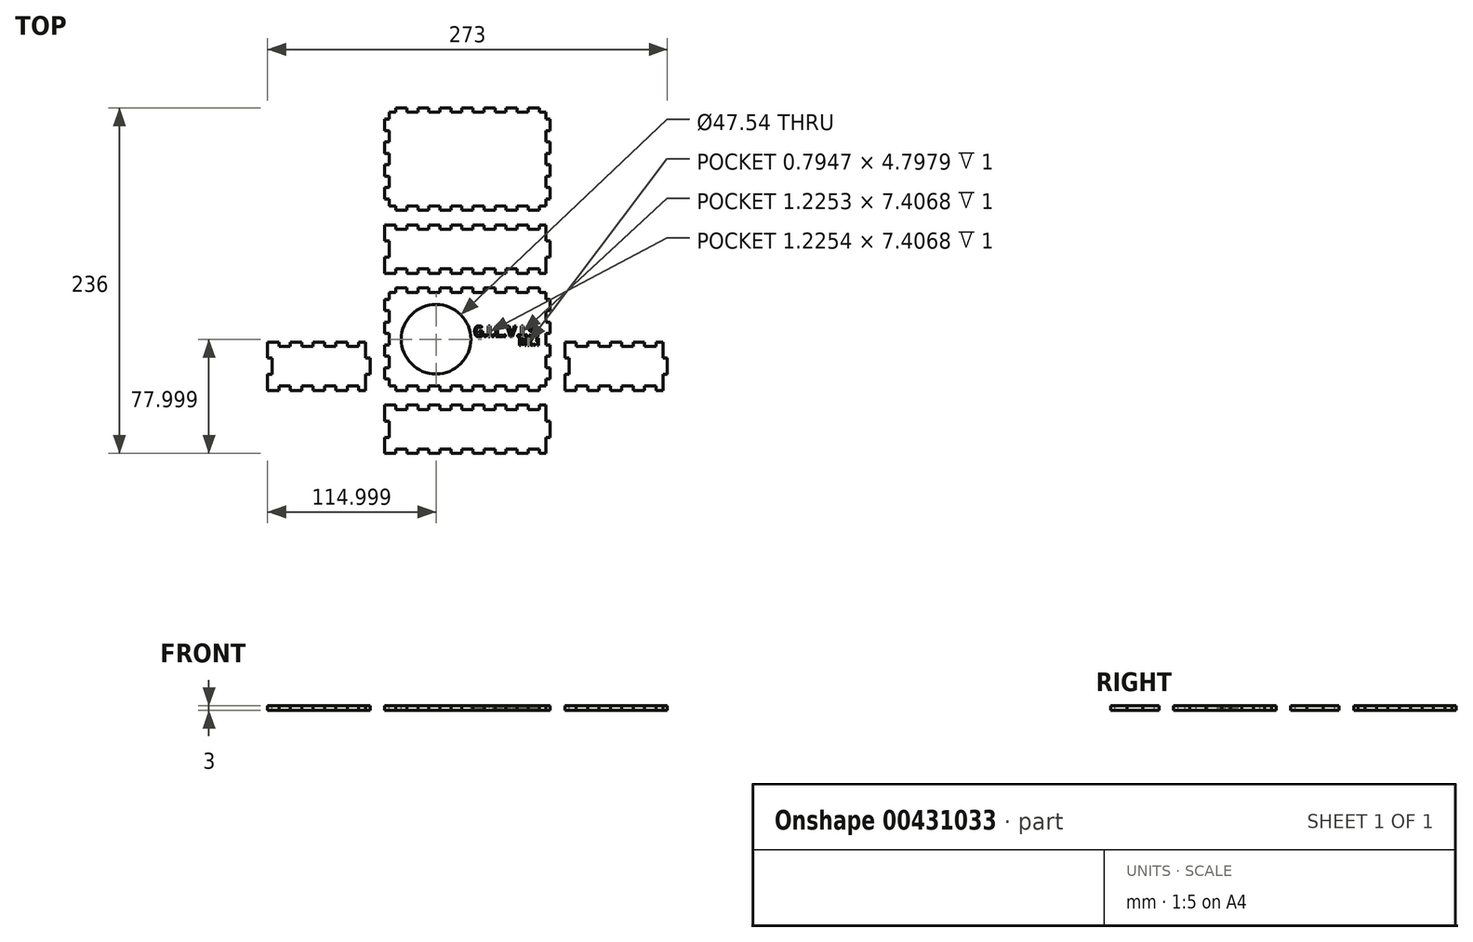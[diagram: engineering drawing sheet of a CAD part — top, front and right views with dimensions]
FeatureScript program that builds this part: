
annotation { "Feature Type Name" : "Feature", "Feature Type Description" : "" }
export const myFeature = defineFeature(function(context is Context, id is Id, definition is map)
    precondition{}
    {
        {
            var Q0;
            Q0=qCreatedBy(makeId("Top.planeOp"),FACE);
            var sketch = newSketch(context, id + "F0", { "sketchPlane" : qUnion([Q0])});
            skLineSegment(sketch, "E0", {"start": v(-136.5, -118) * mm, "end": v(136.5, -118) * mm, "construction": true});
            skLineSegment(sketch, "E1", {"start": v(136.5, -118) * mm, "end": v(136.5, 118) * mm, "construction": true});
            skLineSegment(sketch, "E2", {"start": v(136.5, 118) * mm, "end": v(-136.5, 118) * mm, "construction": true});
            skLineSegment(sketch, "E3", {"start": v(-136.5, 118) * mm, "end": v(-136.5, -118) * mm, "construction": true});
            skLineSegment(sketch, "E4", {"start": v(-56.5, -118) * mm, "end": v(-48.97, -118) * mm});
            skLineSegment(sketch, "E5", {"start": v(-48.97, -115) * mm, "end": v(-48.97, -118) * mm});
            skLineSegment(sketch, "E6", {"start": v(-48.97, -115) * mm, "end": v(-41.43, -115) * mm});
            skLineSegment(sketch, "E7", {"start": v(-41.43, -115) * mm, "end": v(-41.43, -118) * mm});
            skLineSegment(sketch, "E8", {"start": v(-41.43, -118) * mm, "end": v(-33.9, -118) * mm});
            skLineSegment(sketch, "E9", {"start": v(-33.9, -115) * mm, "end": v(-33.9, -118) * mm});
            skLineSegment(sketch, "E10", {"start": v(-33.9, -115) * mm, "end": v(-26.37, -115) * mm});
            skLineSegment(sketch, "E11", {"start": v(-26.37, -115) * mm, "end": v(-26.37, -118) * mm});
            skLineSegment(sketch, "E12", {"start": v(-26.37, -118) * mm, "end": v(-18.83, -118) * mm});
            skLineSegment(sketch, "E13", {"start": v(-18.83, -115) * mm, "end": v(-18.83, -118) * mm});
            skLineSegment(sketch, "E14", {"start": v(-18.83, -115) * mm, "end": v(-11.3, -115) * mm});
            skLineSegment(sketch, "E15", {"start": v(-11.3, -115) * mm, "end": v(-11.3, -118) * mm});
            skLineSegment(sketch, "E16", {"start": v(-11.3, -118) * mm, "end": v(-3.77, -118) * mm});
            skLineSegment(sketch, "E17", {"start": v(-3.77, -115) * mm, "end": v(-3.77, -118) * mm});
            skLineSegment(sketch, "E18", {"start": v(-3.77, -115) * mm, "end": v(3.77, -115) * mm});
            skLineSegment(sketch, "E19", {"start": v(3.77, -115) * mm, "end": v(3.77, -118) * mm});
            skLineSegment(sketch, "E20", {"start": v(3.77, -118) * mm, "end": v(11.3, -118) * mm});
            skLineSegment(sketch, "E21", {"start": v(11.3, -115) * mm, "end": v(11.3, -118) * mm});
            skLineSegment(sketch, "E22", {"start": v(11.3, -115) * mm, "end": v(18.83, -115) * mm});
            skLineSegment(sketch, "E23", {"start": v(18.83, -115) * mm, "end": v(18.83, -118) * mm});
            skLineSegment(sketch, "E24", {"start": v(18.83, -118) * mm, "end": v(26.37, -118) * mm});
            skLineSegment(sketch, "E25", {"start": v(26.37, -115) * mm, "end": v(26.37, -118) * mm});
            skLineSegment(sketch, "E26", {"start": v(26.37, -115) * mm, "end": v(33.9, -115) * mm});
            skLineSegment(sketch, "E27", {"start": v(33.9, -115) * mm, "end": v(33.9, -118) * mm});
            skLineSegment(sketch, "E28", {"start": v(33.9, -118) * mm, "end": v(41.43, -118) * mm});
            skLineSegment(sketch, "E29", {"start": v(41.43, -115) * mm, "end": v(41.43, -118) * mm});
            skLineSegment(sketch, "E30", {"start": v(41.43, -115) * mm, "end": v(48.97, -115) * mm});
            skLineSegment(sketch, "E31", {"start": v(48.97, -115) * mm, "end": v(48.97, -118) * mm});
            skLineSegment(sketch, "E32", {"start": v(48.97, -118) * mm, "end": v(53.5, -118) * mm});
            skLineSegment(sketch, "E33", {"start": v(-56.5, -85) * mm, "end": v(-48.97, -85) * mm});
            skLineSegment(sketch, "E34", {"start": v(-48.97, -85) * mm, "end": v(-48.97, -88) * mm});
            skLineSegment(sketch, "E35", {"start": v(-48.97, -88) * mm, "end": v(-41.43, -88) * mm});
            skLineSegment(sketch, "E36", {"start": v(-41.43, -85) * mm, "end": v(-41.43, -88) * mm});
            skLineSegment(sketch, "E37", {"start": v(-41.43, -85) * mm, "end": v(-33.9, -85) * mm});
            skLineSegment(sketch, "E38", {"start": v(-33.9, -85) * mm, "end": v(-33.9, -88) * mm});
            skLineSegment(sketch, "E39", {"start": v(-33.9, -88) * mm, "end": v(-26.37, -88) * mm});
            skLineSegment(sketch, "E40", {"start": v(-26.37, -85) * mm, "end": v(-26.37, -88) * mm});
            skLineSegment(sketch, "E41", {"start": v(-26.37, -85) * mm, "end": v(-18.83, -85) * mm});
            skLineSegment(sketch, "E42", {"start": v(-18.83, -85) * mm, "end": v(-18.83, -88) * mm});
            skLineSegment(sketch, "E43", {"start": v(-18.83, -88) * mm, "end": v(-11.3, -88) * mm});
            skLineSegment(sketch, "E44", {"start": v(-11.3, -85) * mm, "end": v(-11.3, -88) * mm});
            skLineSegment(sketch, "E45", {"start": v(-11.3, -85) * mm, "end": v(-3.77, -85) * mm});
            skLineSegment(sketch, "E46", {"start": v(-3.77, -85) * mm, "end": v(-3.77, -88) * mm});
            skLineSegment(sketch, "E47", {"start": v(-3.77, -88) * mm, "end": v(3.77, -88) * mm});
            skLineSegment(sketch, "E48", {"start": v(3.77, -85) * mm, "end": v(3.77, -88) * mm});
            skLineSegment(sketch, "E49", {"start": v(3.77, -85) * mm, "end": v(11.3, -85) * mm});
            skLineSegment(sketch, "E50", {"start": v(11.3, -85) * mm, "end": v(11.3, -88) * mm});
            skLineSegment(sketch, "E51", {"start": v(11.3, -88) * mm, "end": v(18.83, -88) * mm});
            skLineSegment(sketch, "E52", {"start": v(18.83, -85) * mm, "end": v(18.83, -88) * mm});
            skLineSegment(sketch, "E53", {"start": v(18.83, -85) * mm, "end": v(26.37, -85) * mm});
            skLineSegment(sketch, "E54", {"start": v(26.37, -85) * mm, "end": v(26.37, -88) * mm});
            skLineSegment(sketch, "E55", {"start": v(26.37, -88) * mm, "end": v(33.9, -88) * mm});
            skLineSegment(sketch, "E56", {"start": v(33.9, -85) * mm, "end": v(33.9, -88) * mm});
            skLineSegment(sketch, "E57", {"start": v(33.9, -85) * mm, "end": v(41.43, -85) * mm});
            skLineSegment(sketch, "E58", {"start": v(41.43, -85) * mm, "end": v(41.43, -88) * mm});
            skLineSegment(sketch, "E59", {"start": v(41.43, -88) * mm, "end": v(48.97, -88) * mm});
            skLineSegment(sketch, "E60", {"start": v(48.97, -85) * mm, "end": v(48.97, -88) * mm});
            skLineSegment(sketch, "E61", {"start": v(48.97, -85) * mm, "end": v(53.5, -85) * mm});
            skLineSegment(sketch, "E62", {"start": v(-56.5, -118) * mm, "end": v(-56.5, -107) * mm});
            skLineSegment(sketch, "E63", {"start": v(-53.5, -107) * mm, "end": v(-56.5, -107) * mm});
            skLineSegment(sketch, "E64", {"start": v(-53.5, -107) * mm, "end": v(-53.5, -96) * mm});
            skLineSegment(sketch, "E65", {"start": v(-53.5, -96) * mm, "end": v(-56.5, -96) * mm});
            skLineSegment(sketch, "E66", {"start": v(-56.5, -96) * mm, "end": v(-56.5, -85) * mm});
            skLineSegment(sketch, "E67", {"start": v(53.5, -118) * mm, "end": v(53.5, -107) * mm});
            skLineSegment(sketch, "E68", {"start": v(56.5, -107) * mm, "end": v(53.5, -107) * mm});
            skLineSegment(sketch, "E69", {"start": v(56.5, -107) * mm, "end": v(56.5, -96) * mm});
            skLineSegment(sketch, "E70", {"start": v(56.5, -96) * mm, "end": v(53.5, -96) * mm});
            skLineSegment(sketch, "E71", {"start": v(53.5, -96) * mm, "end": v(53.5, -85) * mm});
            skLineSegment(sketch, "E72", {"start": v(-136.5, -75) * mm, "end": v(-128.72, -75) * mm});
            skLineSegment(sketch, "E73", {"start": v(-128.72, -72) * mm, "end": v(-128.72, -75) * mm});
            skLineSegment(sketch, "E74", {"start": v(-128.72, -72) * mm, "end": v(-120.94, -72) * mm});
            skLineSegment(sketch, "E75", {"start": v(-120.94, -72) * mm, "end": v(-120.94, -75) * mm});
            skLineSegment(sketch, "E76", {"start": v(-120.94, -75) * mm, "end": v(-113.17, -75) * mm});
            skLineSegment(sketch, "E77", {"start": v(-113.17, -72) * mm, "end": v(-113.17, -75) * mm});
            skLineSegment(sketch, "E78", {"start": v(-113.17, -72) * mm, "end": v(-105.39, -72) * mm});
            skLineSegment(sketch, "E79", {"start": v(-105.39, -72) * mm, "end": v(-105.39, -75) * mm});
            skLineSegment(sketch, "E80", {"start": v(-105.39, -75) * mm, "end": v(-97.61, -75) * mm});
            skLineSegment(sketch, "E81", {"start": v(-97.61, -72) * mm, "end": v(-97.61, -75) * mm});
            skLineSegment(sketch, "E82", {"start": v(-97.61, -72) * mm, "end": v(-89.83, -72) * mm});
            skLineSegment(sketch, "E83", {"start": v(-89.83, -72) * mm, "end": v(-89.83, -75) * mm});
            skLineSegment(sketch, "E84", {"start": v(-89.83, -75) * mm, "end": v(-82.06, -75) * mm});
            skLineSegment(sketch, "E85", {"start": v(-82.06, -72) * mm, "end": v(-82.06, -75) * mm});
            skLineSegment(sketch, "E86", {"start": v(-82.06, -72) * mm, "end": v(-74.28, -72) * mm});
            skLineSegment(sketch, "E87", {"start": v(-74.28, -72) * mm, "end": v(-74.28, -75) * mm});
            skLineSegment(sketch, "E88", {"start": v(-74.28, -75) * mm, "end": v(-69.5, -75) * mm});
            skLineSegment(sketch, "E89", {"start": v(-136.5, -42) * mm, "end": v(-128.72, -42) * mm});
            skLineSegment(sketch, "E90", {"start": v(-128.72, -42) * mm, "end": v(-128.72, -45) * mm});
            skLineSegment(sketch, "E91", {"start": v(-128.72, -45) * mm, "end": v(-120.94, -45) * mm});
            skLineSegment(sketch, "E92", {"start": v(-120.94, -42) * mm, "end": v(-120.94, -45) * mm});
            skLineSegment(sketch, "E93", {"start": v(-120.94, -42) * mm, "end": v(-113.17, -42) * mm});
            skLineSegment(sketch, "E94", {"start": v(-113.17, -42) * mm, "end": v(-113.17, -45) * mm});
            skLineSegment(sketch, "E95", {"start": v(-113.17, -45) * mm, "end": v(-105.39, -45) * mm});
            skLineSegment(sketch, "E96", {"start": v(-105.39, -42) * mm, "end": v(-105.39, -45) * mm});
            skLineSegment(sketch, "E97", {"start": v(-105.39, -42) * mm, "end": v(-97.61, -42) * mm});
            skLineSegment(sketch, "E98", {"start": v(-97.61, -42) * mm, "end": v(-97.61, -45) * mm});
            skLineSegment(sketch, "E99", {"start": v(-97.61, -45) * mm, "end": v(-89.83, -45) * mm});
            skLineSegment(sketch, "E100", {"start": v(-89.83, -42) * mm, "end": v(-89.83, -45) * mm});
            skLineSegment(sketch, "E101", {"start": v(-89.83, -42) * mm, "end": v(-82.06, -42) * mm});
            skLineSegment(sketch, "E102", {"start": v(-82.06, -42) * mm, "end": v(-82.06, -45) * mm});
            skLineSegment(sketch, "E103", {"start": v(-82.06, -45) * mm, "end": v(-74.28, -45) * mm});
            skLineSegment(sketch, "E104", {"start": v(-74.28, -42) * mm, "end": v(-74.28, -45) * mm});
            skLineSegment(sketch, "E105", {"start": v(-74.28, -42) * mm, "end": v(-69.5, -42) * mm});
            skLineSegment(sketch, "E106", {"start": v(-136.5, -75) * mm, "end": v(-136.5, -64) * mm});
            skLineSegment(sketch, "E107", {"start": v(-133.5, -64) * mm, "end": v(-136.5, -64) * mm});
            skLineSegment(sketch, "E108", {"start": v(-133.5, -64) * mm, "end": v(-133.5, -53) * mm});
            skLineSegment(sketch, "E109", {"start": v(-133.5, -53) * mm, "end": v(-136.5, -53) * mm});
            skLineSegment(sketch, "E110", {"start": v(-136.5, -53) * mm, "end": v(-136.5, -42) * mm});
            skLineSegment(sketch, "E111", {"start": v(-69.5, -75) * mm, "end": v(-69.5, -64) * mm});
            skLineSegment(sketch, "E112", {"start": v(-66.5, -64) * mm, "end": v(-69.5, -64) * mm});
            skLineSegment(sketch, "E113", {"start": v(-66.5, -64) * mm, "end": v(-66.5, -53) * mm});
            skLineSegment(sketch, "E114", {"start": v(-66.5, -53) * mm, "end": v(-69.5, -53) * mm});
            skLineSegment(sketch, "E115", {"start": v(-69.5, -53) * mm, "end": v(-69.5, -42) * mm});
            skLineSegment(sketch, "E116", {"start": v(-53.5, -72) * mm, "end": v(-48.97, -72) * mm});
            skLineSegment(sketch, "E117", {"start": v(-48.97, -72) * mm, "end": v(-48.97, -75) * mm});
            skLineSegment(sketch, "E118", {"start": v(-48.97, -75) * mm, "end": v(-41.43, -75) * mm});
            skLineSegment(sketch, "E119", {"start": v(-41.43, -72) * mm, "end": v(-41.43, -75) * mm});
            skLineSegment(sketch, "E120", {"start": v(-41.43, -72) * mm, "end": v(-33.9, -72) * mm});
            skLineSegment(sketch, "E121", {"start": v(-33.9, -72) * mm, "end": v(-33.9, -75) * mm});
            skLineSegment(sketch, "E122", {"start": v(-33.9, -75) * mm, "end": v(-26.37, -75) * mm});
            skLineSegment(sketch, "E123", {"start": v(-26.37, -72) * mm, "end": v(-26.37, -75) * mm});
            skLineSegment(sketch, "E124", {"start": v(-26.37, -72) * mm, "end": v(-18.83, -72) * mm});
            skLineSegment(sketch, "E125", {"start": v(-18.83, -72) * mm, "end": v(-18.83, -75) * mm});
            skLineSegment(sketch, "E126", {"start": v(-18.83, -75) * mm, "end": v(-11.3, -75) * mm});
            skLineSegment(sketch, "E127", {"start": v(-11.3, -72) * mm, "end": v(-11.3, -75) * mm});
            skLineSegment(sketch, "E128", {"start": v(-11.3, -72) * mm, "end": v(-3.77, -72) * mm});
            skLineSegment(sketch, "E129", {"start": v(-3.77, -72) * mm, "end": v(-3.77, -75) * mm});
            skLineSegment(sketch, "E130", {"start": v(-3.77, -75) * mm, "end": v(3.77, -75) * mm});
            skLineSegment(sketch, "E131", {"start": v(3.77, -72) * mm, "end": v(3.77, -75) * mm});
            skLineSegment(sketch, "E132", {"start": v(3.77, -72) * mm, "end": v(11.3, -72) * mm});
            skLineSegment(sketch, "E133", {"start": v(11.3, -72) * mm, "end": v(11.3, -75) * mm});
            skLineSegment(sketch, "E134", {"start": v(11.3, -75) * mm, "end": v(18.83, -75) * mm});
            skLineSegment(sketch, "E135", {"start": v(18.83, -72) * mm, "end": v(18.83, -75) * mm});
            skLineSegment(sketch, "E136", {"start": v(18.83, -72) * mm, "end": v(26.37, -72) * mm});
            skLineSegment(sketch, "E137", {"start": v(26.37, -72) * mm, "end": v(26.37, -75) * mm});
            skLineSegment(sketch, "E138", {"start": v(26.37, -75) * mm, "end": v(33.9, -75) * mm});
            skLineSegment(sketch, "E139", {"start": v(33.9, -72) * mm, "end": v(33.9, -75) * mm});
            skLineSegment(sketch, "E140", {"start": v(33.9, -72) * mm, "end": v(41.43, -72) * mm});
            skLineSegment(sketch, "E141", {"start": v(41.43, -72) * mm, "end": v(41.43, -75) * mm});
            skLineSegment(sketch, "E142", {"start": v(41.43, -75) * mm, "end": v(48.97, -75) * mm});
            skLineSegment(sketch, "E143", {"start": v(48.97, -72) * mm, "end": v(48.97, -75) * mm});
            skLineSegment(sketch, "E144", {"start": v(48.97, -72) * mm, "end": v(53.5, -72) * mm});
            skLineSegment(sketch, "E145", {"start": v(-53.5, -8) * mm, "end": v(-48.97, -8) * mm});
            skLineSegment(sketch, "E146", {"start": v(-48.97, -5) * mm, "end": v(-48.97, -8) * mm});
            skLineSegment(sketch, "E147", {"start": v(-48.97, -5) * mm, "end": v(-41.43, -5) * mm});
            skLineSegment(sketch, "E148", {"start": v(-41.43, -5) * mm, "end": v(-41.43, -8) * mm});
            skLineSegment(sketch, "E149", {"start": v(-41.43, -8) * mm, "end": v(-33.9, -8) * mm});
            skLineSegment(sketch, "E150", {"start": v(-33.9, -5) * mm, "end": v(-33.9, -8) * mm});
            skLineSegment(sketch, "E151", {"start": v(-33.9, -5) * mm, "end": v(-26.37, -5) * mm});
            skLineSegment(sketch, "E152", {"start": v(-26.37, -5) * mm, "end": v(-26.37, -8) * mm});
            skLineSegment(sketch, "E153", {"start": v(-26.37, -8) * mm, "end": v(-18.83, -8) * mm});
            skLineSegment(sketch, "E154", {"start": v(-18.83, -5) * mm, "end": v(-18.83, -8) * mm});
            skLineSegment(sketch, "E155", {"start": v(-18.83, -5) * mm, "end": v(-11.3, -5) * mm});
            skLineSegment(sketch, "E156", {"start": v(-11.3, -5) * mm, "end": v(-11.3, -8) * mm});
            skLineSegment(sketch, "E157", {"start": v(-11.3, -8) * mm, "end": v(-3.77, -8) * mm});
            skLineSegment(sketch, "E158", {"start": v(-3.77, -5) * mm, "end": v(-3.77, -8) * mm});
            skLineSegment(sketch, "E159", {"start": v(-3.77, -5) * mm, "end": v(3.77, -5) * mm});
            skLineSegment(sketch, "E160", {"start": v(3.77, -5) * mm, "end": v(3.77, -8) * mm});
            skLineSegment(sketch, "E161", {"start": v(3.77, -8) * mm, "end": v(11.3, -8) * mm});
            skLineSegment(sketch, "E162", {"start": v(11.3, -5) * mm, "end": v(11.3, -8) * mm});
            skLineSegment(sketch, "E163", {"start": v(11.3, -5) * mm, "end": v(18.83, -5) * mm});
            skLineSegment(sketch, "E164", {"start": v(18.83, -5) * mm, "end": v(18.83, -8) * mm});
            skLineSegment(sketch, "E165", {"start": v(18.83, -8) * mm, "end": v(26.37, -8) * mm});
            skLineSegment(sketch, "E166", {"start": v(26.37, -5) * mm, "end": v(26.37, -8) * mm});
            skLineSegment(sketch, "E167", {"start": v(26.37, -5) * mm, "end": v(33.9, -5) * mm});
            skLineSegment(sketch, "E168", {"start": v(33.9, -5) * mm, "end": v(33.9, -8) * mm});
            skLineSegment(sketch, "E169", {"start": v(33.9, -8) * mm, "end": v(41.43, -8) * mm});
            skLineSegment(sketch, "E170", {"start": v(41.43, -5) * mm, "end": v(41.43, -8) * mm});
            skLineSegment(sketch, "E171", {"start": v(41.43, -5) * mm, "end": v(48.97, -5) * mm});
            skLineSegment(sketch, "E172", {"start": v(48.97, -5) * mm, "end": v(48.97, -8) * mm});
            skLineSegment(sketch, "E173", {"start": v(48.97, -8) * mm, "end": v(53.5, -8) * mm});
            skLineSegment(sketch, "E174", {"start": v(-53.5, -72) * mm, "end": v(-53.5, -67.22) * mm});
            skLineSegment(sketch, "E175", {"start": v(-53.5, -67.22) * mm, "end": v(-56.5, -67.22) * mm});
            skLineSegment(sketch, "E176", {"start": v(-56.5, -67.22) * mm, "end": v(-56.5, -59.44) * mm});
            skLineSegment(sketch, "E177", {"start": v(-53.5, -59.44) * mm, "end": v(-56.5, -59.44) * mm});
            skLineSegment(sketch, "E178", {"start": v(-53.5, -59.44) * mm, "end": v(-53.5, -51.67) * mm});
            skLineSegment(sketch, "E179", {"start": v(-53.5, -51.67) * mm, "end": v(-56.5, -51.67) * mm});
            skLineSegment(sketch, "E180", {"start": v(-56.5, -51.67) * mm, "end": v(-56.5, -43.89) * mm});
            skLineSegment(sketch, "E181", {"start": v(-53.5, -43.89) * mm, "end": v(-56.5, -43.89) * mm});
            skLineSegment(sketch, "E182", {"start": v(-53.5, -43.89) * mm, "end": v(-53.5, -36.11) * mm});
            skLineSegment(sketch, "E183", {"start": v(-53.5, -36.11) * mm, "end": v(-56.5, -36.11) * mm});
            skLineSegment(sketch, "E184", {"start": v(-56.5, -36.11) * mm, "end": v(-56.5, -28.33) * mm});
            skLineSegment(sketch, "E185", {"start": v(-53.5, -28.33) * mm, "end": v(-56.5, -28.33) * mm});
            skLineSegment(sketch, "E186", {"start": v(-53.5, -28.33) * mm, "end": v(-53.5, -20.56) * mm});
            skLineSegment(sketch, "E187", {"start": v(-53.5, -20.56) * mm, "end": v(-56.5, -20.56) * mm});
            skLineSegment(sketch, "E188", {"start": v(-56.5, -20.56) * mm, "end": v(-56.5, -12.78) * mm});
            skLineSegment(sketch, "E189", {"start": v(-53.5, -12.78) * mm, "end": v(-56.5, -12.78) * mm});
            skLineSegment(sketch, "E190", {"start": v(-53.5, -12.78) * mm, "end": v(-53.5, -8) * mm});
            skLineSegment(sketch, "E191", {"start": v(53.5, -72) * mm, "end": v(53.5, -67.22) * mm});
            skLineSegment(sketch, "E192", {"start": v(56.5, -67.22) * mm, "end": v(53.5, -67.22) * mm});
            skLineSegment(sketch, "E193", {"start": v(56.5, -67.22) * mm, "end": v(56.5, -59.44) * mm});
            skLineSegment(sketch, "E194", {"start": v(56.5, -59.44) * mm, "end": v(53.5, -59.44) * mm});
            skLineSegment(sketch, "E195", {"start": v(53.5, -59.44) * mm, "end": v(53.5, -51.67) * mm});
            skLineSegment(sketch, "E196", {"start": v(56.5, -51.67) * mm, "end": v(53.5, -51.67) * mm});
            skLineSegment(sketch, "E197", {"start": v(56.5, -51.67) * mm, "end": v(56.5, -43.89) * mm});
            skLineSegment(sketch, "E198", {"start": v(56.5, -43.89) * mm, "end": v(53.5, -43.89) * mm});
            skLineSegment(sketch, "E199", {"start": v(53.5, -43.89) * mm, "end": v(53.5, -36.11) * mm});
            skLineSegment(sketch, "E200", {"start": v(56.5, -36.11) * mm, "end": v(53.5, -36.11) * mm});
            skLineSegment(sketch, "E201", {"start": v(56.5, -36.11) * mm, "end": v(56.5, -28.33) * mm});
            skLineSegment(sketch, "E202", {"start": v(56.5, -28.33) * mm, "end": v(53.5, -28.33) * mm});
            skLineSegment(sketch, "E203", {"start": v(53.5, -28.33) * mm, "end": v(53.5, -20.56) * mm});
            skLineSegment(sketch, "E204", {"start": v(56.5, -20.56) * mm, "end": v(53.5, -20.56) * mm});
            skLineSegment(sketch, "E205", {"start": v(56.5, -20.56) * mm, "end": v(56.5, -12.78) * mm});
            skLineSegment(sketch, "E206", {"start": v(56.5, -12.78) * mm, "end": v(53.5, -12.78) * mm});
            skLineSegment(sketch, "E207", {"start": v(53.5, -12.78) * mm, "end": v(53.5, -8) * mm});
            skLineSegment(sketch, "E208", {"start": v(66.5, -75) * mm, "end": v(74.28, -75) * mm});
            skLineSegment(sketch, "E209", {"start": v(74.28, -72) * mm, "end": v(74.28, -75) * mm});
            skLineSegment(sketch, "E210", {"start": v(74.28, -72) * mm, "end": v(82.06, -72) * mm});
            skLineSegment(sketch, "E211", {"start": v(82.06, -72) * mm, "end": v(82.06, -75) * mm});
            skLineSegment(sketch, "E212", {"start": v(82.06, -75) * mm, "end": v(89.83, -75) * mm});
            skLineSegment(sketch, "E213", {"start": v(89.83, -72) * mm, "end": v(89.83, -75) * mm});
            skLineSegment(sketch, "E214", {"start": v(89.83, -72) * mm, "end": v(97.61, -72) * mm});
            skLineSegment(sketch, "E215", {"start": v(97.61, -72) * mm, "end": v(97.61, -75) * mm});
            skLineSegment(sketch, "E216", {"start": v(97.61, -75) * mm, "end": v(105.39, -75) * mm});
            skLineSegment(sketch, "E217", {"start": v(105.39, -72) * mm, "end": v(105.39, -75) * mm});
            skLineSegment(sketch, "E218", {"start": v(105.39, -72) * mm, "end": v(113.17, -72) * mm});
            skLineSegment(sketch, "E219", {"start": v(113.17, -72) * mm, "end": v(113.17, -75) * mm});
            skLineSegment(sketch, "E220", {"start": v(113.17, -75) * mm, "end": v(120.94, -75) * mm});
            skLineSegment(sketch, "E221", {"start": v(120.94, -72) * mm, "end": v(120.94, -75) * mm});
            skLineSegment(sketch, "E222", {"start": v(120.94, -72) * mm, "end": v(128.72, -72) * mm});
            skLineSegment(sketch, "E223", {"start": v(128.72, -72) * mm, "end": v(128.72, -75) * mm});
            skLineSegment(sketch, "E224", {"start": v(128.72, -75) * mm, "end": v(133.5, -75) * mm});
            skLineSegment(sketch, "E225", {"start": v(66.5, -42) * mm, "end": v(74.28, -42) * mm});
            skLineSegment(sketch, "E226", {"start": v(74.28, -42) * mm, "end": v(74.28, -45) * mm});
            skLineSegment(sketch, "E227", {"start": v(74.28, -45) * mm, "end": v(82.06, -45) * mm});
            skLineSegment(sketch, "E228", {"start": v(82.06, -42) * mm, "end": v(82.06, -45) * mm});
            skLineSegment(sketch, "E229", {"start": v(82.06, -42) * mm, "end": v(89.83, -42) * mm});
            skLineSegment(sketch, "E230", {"start": v(89.83, -42) * mm, "end": v(89.83, -45) * mm});
            skLineSegment(sketch, "E231", {"start": v(89.83, -45) * mm, "end": v(97.61, -45) * mm});
            skLineSegment(sketch, "E232", {"start": v(97.61, -42) * mm, "end": v(97.61, -45) * mm});
            skLineSegment(sketch, "E233", {"start": v(97.61, -42) * mm, "end": v(105.39, -42) * mm});
            skLineSegment(sketch, "E234", {"start": v(105.39, -42) * mm, "end": v(105.39, -45) * mm});
            skLineSegment(sketch, "E235", {"start": v(105.39, -45) * mm, "end": v(113.17, -45) * mm});
            skLineSegment(sketch, "E236", {"start": v(113.17, -42) * mm, "end": v(113.17, -45) * mm});
            skLineSegment(sketch, "E237", {"start": v(113.17, -42) * mm, "end": v(120.94, -42) * mm});
            skLineSegment(sketch, "E238", {"start": v(120.94, -42) * mm, "end": v(120.94, -45) * mm});
            skLineSegment(sketch, "E239", {"start": v(120.94, -45) * mm, "end": v(128.72, -45) * mm});
            skLineSegment(sketch, "E240", {"start": v(128.72, -42) * mm, "end": v(128.72, -45) * mm});
            skLineSegment(sketch, "E241", {"start": v(128.72, -42) * mm, "end": v(133.5, -42) * mm});
            skLineSegment(sketch, "E242", {"start": v(66.5, -75) * mm, "end": v(66.5, -64) * mm});
            skLineSegment(sketch, "E243", {"start": v(69.5, -64) * mm, "end": v(66.5, -64) * mm});
            skLineSegment(sketch, "E244", {"start": v(69.5, -64) * mm, "end": v(69.5, -53) * mm});
            skLineSegment(sketch, "E245", {"start": v(69.5, -53) * mm, "end": v(66.5, -53) * mm});
            skLineSegment(sketch, "E246", {"start": v(66.5, -53) * mm, "end": v(66.5, -42) * mm});
            skLineSegment(sketch, "E247", {"start": v(133.5, -75) * mm, "end": v(133.5, -64) * mm});
            skLineSegment(sketch, "E248", {"start": v(136.5, -64) * mm, "end": v(133.5, -64) * mm});
            skLineSegment(sketch, "E249", {"start": v(136.5, -64) * mm, "end": v(136.5, -53) * mm});
            skLineSegment(sketch, "E250", {"start": v(136.5, -53) * mm, "end": v(133.5, -53) * mm});
            skLineSegment(sketch, "E251", {"start": v(133.5, -53) * mm, "end": v(133.5, -42) * mm});
            skLineSegment(sketch, "E252", {"start": v(-56.5, 5) * mm, "end": v(-48.97, 5) * mm});
            skLineSegment(sketch, "E253", {"start": v(-48.97, 8) * mm, "end": v(-48.97, 5) * mm});
            skLineSegment(sketch, "E254", {"start": v(-48.97, 8) * mm, "end": v(-41.43, 8) * mm});
            skLineSegment(sketch, "E255", {"start": v(-41.43, 8) * mm, "end": v(-41.43, 5) * mm});
            skLineSegment(sketch, "E256", {"start": v(-41.43, 5) * mm, "end": v(-33.9, 5) * mm});
            skLineSegment(sketch, "E257", {"start": v(-33.9, 8) * mm, "end": v(-33.9, 5) * mm});
            skLineSegment(sketch, "E258", {"start": v(-33.9, 8) * mm, "end": v(-26.37, 8) * mm});
            skLineSegment(sketch, "E259", {"start": v(-26.37, 8) * mm, "end": v(-26.37, 5) * mm});
            skLineSegment(sketch, "E260", {"start": v(-26.37, 5) * mm, "end": v(-18.83, 5) * mm});
            skLineSegment(sketch, "E261", {"start": v(-18.83, 8) * mm, "end": v(-18.83, 5) * mm});
            skLineSegment(sketch, "E262", {"start": v(-18.83, 8) * mm, "end": v(-11.3, 8) * mm});
            skLineSegment(sketch, "E263", {"start": v(-11.3, 8) * mm, "end": v(-11.3, 5) * mm});
            skLineSegment(sketch, "E264", {"start": v(-11.3, 5) * mm, "end": v(-3.77, 5) * mm});
            skLineSegment(sketch, "E265", {"start": v(-3.77, 8) * mm, "end": v(-3.77, 5) * mm});
            skLineSegment(sketch, "E266", {"start": v(-3.77, 8) * mm, "end": v(3.77, 8) * mm});
            skLineSegment(sketch, "E267", {"start": v(3.77, 8) * mm, "end": v(3.77, 5) * mm});
            skLineSegment(sketch, "E268", {"start": v(3.77, 5) * mm, "end": v(11.3, 5) * mm});
            skLineSegment(sketch, "E269", {"start": v(11.3, 8) * mm, "end": v(11.3, 5) * mm});
            skLineSegment(sketch, "E270", {"start": v(11.3, 8) * mm, "end": v(18.83, 8) * mm});
            skLineSegment(sketch, "E271", {"start": v(18.83, 8) * mm, "end": v(18.83, 5) * mm});
            skLineSegment(sketch, "E272", {"start": v(18.83, 5) * mm, "end": v(26.37, 5) * mm});
            skLineSegment(sketch, "E273", {"start": v(26.37, 8) * mm, "end": v(26.37, 5) * mm});
            skLineSegment(sketch, "E274", {"start": v(26.37, 8) * mm, "end": v(33.9, 8) * mm});
            skLineSegment(sketch, "E275", {"start": v(33.9, 8) * mm, "end": v(33.9, 5) * mm});
            skLineSegment(sketch, "E276", {"start": v(33.9, 5) * mm, "end": v(41.43, 5) * mm});
            skLineSegment(sketch, "E277", {"start": v(41.43, 8) * mm, "end": v(41.43, 5) * mm});
            skLineSegment(sketch, "E278", {"start": v(41.43, 8) * mm, "end": v(48.97, 8) * mm});
            skLineSegment(sketch, "E279", {"start": v(48.97, 8) * mm, "end": v(48.97, 5) * mm});
            skLineSegment(sketch, "E280", {"start": v(48.97, 5) * mm, "end": v(53.5, 5) * mm});
            skLineSegment(sketch, "E281", {"start": v(-56.5, 38) * mm, "end": v(-48.97, 38) * mm});
            skLineSegment(sketch, "E282", {"start": v(-48.97, 38) * mm, "end": v(-48.97, 35) * mm});
            skLineSegment(sketch, "E283", {"start": v(-48.97, 35) * mm, "end": v(-41.43, 35) * mm});
            skLineSegment(sketch, "E284", {"start": v(-41.43, 38) * mm, "end": v(-41.43, 35) * mm});
            skLineSegment(sketch, "E285", {"start": v(-41.43, 38) * mm, "end": v(-33.9, 38) * mm});
            skLineSegment(sketch, "E286", {"start": v(-33.9, 38) * mm, "end": v(-33.9, 35) * mm});
            skLineSegment(sketch, "E287", {"start": v(-33.9, 35) * mm, "end": v(-26.37, 35) * mm});
            skLineSegment(sketch, "E288", {"start": v(-26.37, 38) * mm, "end": v(-26.37, 35) * mm});
            skLineSegment(sketch, "E289", {"start": v(-26.37, 38) * mm, "end": v(-18.83, 38) * mm});
            skLineSegment(sketch, "E290", {"start": v(-18.83, 38) * mm, "end": v(-18.83, 35) * mm});
            skLineSegment(sketch, "E291", {"start": v(-18.83, 35) * mm, "end": v(-11.3, 35) * mm});
            skLineSegment(sketch, "E292", {"start": v(-11.3, 38) * mm, "end": v(-11.3, 35) * mm});
            skLineSegment(sketch, "E293", {"start": v(-11.3, 38) * mm, "end": v(-3.77, 38) * mm});
            skLineSegment(sketch, "E294", {"start": v(-3.77, 38) * mm, "end": v(-3.77, 35) * mm});
            skLineSegment(sketch, "E295", {"start": v(-3.77, 35) * mm, "end": v(3.77, 35) * mm});
            skLineSegment(sketch, "E296", {"start": v(3.77, 38) * mm, "end": v(3.77, 35) * mm});
            skLineSegment(sketch, "E297", {"start": v(3.77, 38) * mm, "end": v(11.3, 38) * mm});
            skLineSegment(sketch, "E298", {"start": v(11.3, 38) * mm, "end": v(11.3, 35) * mm});
            skLineSegment(sketch, "E299", {"start": v(11.3, 35) * mm, "end": v(18.83, 35) * mm});
            skLineSegment(sketch, "E300", {"start": v(18.83, 38) * mm, "end": v(18.83, 35) * mm});
            skLineSegment(sketch, "E301", {"start": v(18.83, 38) * mm, "end": v(26.37, 38) * mm});
            skLineSegment(sketch, "E302", {"start": v(26.37, 38) * mm, "end": v(26.37, 35) * mm});
            skLineSegment(sketch, "E303", {"start": v(26.37, 35) * mm, "end": v(33.9, 35) * mm});
            skLineSegment(sketch, "E304", {"start": v(33.9, 38) * mm, "end": v(33.9, 35) * mm});
            skLineSegment(sketch, "E305", {"start": v(33.9, 38) * mm, "end": v(41.43, 38) * mm});
            skLineSegment(sketch, "E306", {"start": v(41.43, 38) * mm, "end": v(41.43, 35) * mm});
            skLineSegment(sketch, "E307", {"start": v(41.43, 35) * mm, "end": v(48.97, 35) * mm});
            skLineSegment(sketch, "E308", {"start": v(48.97, 38) * mm, "end": v(48.97, 35) * mm});
            skLineSegment(sketch, "E309", {"start": v(48.97, 38) * mm, "end": v(53.5, 38) * mm});
            skLineSegment(sketch, "E310", {"start": v(-56.5, 5) * mm, "end": v(-56.5, 16) * mm});
            skLineSegment(sketch, "E311", {"start": v(-53.5, 16) * mm, "end": v(-56.5, 16) * mm});
            skLineSegment(sketch, "E312", {"start": v(-53.5, 16) * mm, "end": v(-53.5, 27) * mm});
            skLineSegment(sketch, "E313", {"start": v(-53.5, 27) * mm, "end": v(-56.5, 27) * mm});
            skLineSegment(sketch, "E314", {"start": v(-56.5, 27) * mm, "end": v(-56.5, 38) * mm});
            skLineSegment(sketch, "E315", {"start": v(53.5, 5) * mm, "end": v(53.5, 16) * mm});
            skLineSegment(sketch, "E316", {"start": v(56.5, 16) * mm, "end": v(53.5, 16) * mm});
            skLineSegment(sketch, "E317", {"start": v(56.5, 16) * mm, "end": v(56.5, 27) * mm});
            skLineSegment(sketch, "E318", {"start": v(56.5, 27) * mm, "end": v(53.5, 27) * mm});
            skLineSegment(sketch, "E319", {"start": v(53.5, 27) * mm, "end": v(53.5, 38) * mm});
            skLineSegment(sketch, "E320", {"start": v(-53.5, 51) * mm, "end": v(-48.97, 51) * mm});
            skLineSegment(sketch, "E321", {"start": v(-48.97, 51) * mm, "end": v(-48.97, 48) * mm});
            skLineSegment(sketch, "E322", {"start": v(-48.97, 48) * mm, "end": v(-41.43, 48) * mm});
            skLineSegment(sketch, "E323", {"start": v(-41.43, 51) * mm, "end": v(-41.43, 48) * mm});
            skLineSegment(sketch, "E324", {"start": v(-41.43, 51) * mm, "end": v(-33.9, 51) * mm});
            skLineSegment(sketch, "E325", {"start": v(-33.9, 51) * mm, "end": v(-33.9, 48) * mm});
            skLineSegment(sketch, "E326", {"start": v(-33.9, 48) * mm, "end": v(-26.37, 48) * mm});
            skLineSegment(sketch, "E327", {"start": v(-26.37, 51) * mm, "end": v(-26.37, 48) * mm});
            skLineSegment(sketch, "E328", {"start": v(-26.37, 51) * mm, "end": v(-18.83, 51) * mm});
            skLineSegment(sketch, "E329", {"start": v(-18.83, 51) * mm, "end": v(-18.83, 48) * mm});
            skLineSegment(sketch, "E330", {"start": v(-18.83, 48) * mm, "end": v(-11.3, 48) * mm});
            skLineSegment(sketch, "E331", {"start": v(-11.3, 51) * mm, "end": v(-11.3, 48) * mm});
            skLineSegment(sketch, "E332", {"start": v(-11.3, 51) * mm, "end": v(-3.77, 51) * mm});
            skLineSegment(sketch, "E333", {"start": v(-3.77, 51) * mm, "end": v(-3.77, 48) * mm});
            skLineSegment(sketch, "E334", {"start": v(-3.77, 48) * mm, "end": v(3.77, 48) * mm});
            skLineSegment(sketch, "E335", {"start": v(3.77, 51) * mm, "end": v(3.77, 48) * mm});
            skLineSegment(sketch, "E336", {"start": v(3.77, 51) * mm, "end": v(11.3, 51) * mm});
            skLineSegment(sketch, "E337", {"start": v(11.3, 51) * mm, "end": v(11.3, 48) * mm});
            skLineSegment(sketch, "E338", {"start": v(11.3, 48) * mm, "end": v(18.83, 48) * mm});
            skLineSegment(sketch, "E339", {"start": v(18.83, 51) * mm, "end": v(18.83, 48) * mm});
            skLineSegment(sketch, "E340", {"start": v(18.83, 51) * mm, "end": v(26.37, 51) * mm});
            skLineSegment(sketch, "E341", {"start": v(26.37, 51) * mm, "end": v(26.37, 48) * mm});
            skLineSegment(sketch, "E342", {"start": v(26.37, 48) * mm, "end": v(33.9, 48) * mm});
            skLineSegment(sketch, "E343", {"start": v(33.9, 51) * mm, "end": v(33.9, 48) * mm});
            skLineSegment(sketch, "E344", {"start": v(33.9, 51) * mm, "end": v(41.43, 51) * mm});
            skLineSegment(sketch, "E345", {"start": v(41.43, 51) * mm, "end": v(41.43, 48) * mm});
            skLineSegment(sketch, "E346", {"start": v(41.43, 48) * mm, "end": v(48.97, 48) * mm});
            skLineSegment(sketch, "E347", {"start": v(48.97, 51) * mm, "end": v(48.97, 48) * mm});
            skLineSegment(sketch, "E348", {"start": v(48.97, 51) * mm, "end": v(53.5, 51) * mm});
            skLineSegment(sketch, "E349", {"start": v(-53.5, 115) * mm, "end": v(-48.97, 115) * mm});
            skLineSegment(sketch, "E350", {"start": v(-48.97, 118) * mm, "end": v(-48.97, 115) * mm});
            skLineSegment(sketch, "E351", {"start": v(-48.97, 118) * mm, "end": v(-41.43, 118) * mm});
            skLineSegment(sketch, "E352", {"start": v(-41.43, 118) * mm, "end": v(-41.43, 115) * mm});
            skLineSegment(sketch, "E353", {"start": v(-41.43, 115) * mm, "end": v(-33.9, 115) * mm});
            skLineSegment(sketch, "E354", {"start": v(-33.9, 118) * mm, "end": v(-33.9, 115) * mm});
            skLineSegment(sketch, "E355", {"start": v(-33.9, 118) * mm, "end": v(-26.37, 118) * mm});
            skLineSegment(sketch, "E356", {"start": v(-26.37, 118) * mm, "end": v(-26.37, 115) * mm});
            skLineSegment(sketch, "E357", {"start": v(-26.37, 115) * mm, "end": v(-18.83, 115) * mm});
            skLineSegment(sketch, "E358", {"start": v(-18.83, 118) * mm, "end": v(-18.83, 115) * mm});
            skLineSegment(sketch, "E359", {"start": v(-18.83, 118) * mm, "end": v(-11.3, 118) * mm});
            skLineSegment(sketch, "E360", {"start": v(-11.3, 118) * mm, "end": v(-11.3, 115) * mm});
            skLineSegment(sketch, "E361", {"start": v(-11.3, 115) * mm, "end": v(-3.77, 115) * mm});
            skLineSegment(sketch, "E362", {"start": v(-3.77, 118) * mm, "end": v(-3.77, 115) * mm});
            skLineSegment(sketch, "E363", {"start": v(-3.77, 118) * mm, "end": v(3.77, 118) * mm});
            skLineSegment(sketch, "E364", {"start": v(3.77, 118) * mm, "end": v(3.77, 115) * mm});
            skLineSegment(sketch, "E365", {"start": v(3.77, 115) * mm, "end": v(11.3, 115) * mm});
            skLineSegment(sketch, "E366", {"start": v(11.3, 118) * mm, "end": v(11.3, 115) * mm});
            skLineSegment(sketch, "E367", {"start": v(11.3, 118) * mm, "end": v(18.83, 118) * mm});
            skLineSegment(sketch, "E368", {"start": v(18.83, 118) * mm, "end": v(18.83, 115) * mm});
            skLineSegment(sketch, "E369", {"start": v(18.83, 115) * mm, "end": v(26.37, 115) * mm});
            skLineSegment(sketch, "E370", {"start": v(26.37, 118) * mm, "end": v(26.37, 115) * mm});
            skLineSegment(sketch, "E371", {"start": v(26.37, 118) * mm, "end": v(33.9, 118) * mm});
            skLineSegment(sketch, "E372", {"start": v(33.9, 118) * mm, "end": v(33.9, 115) * mm});
            skLineSegment(sketch, "E373", {"start": v(33.9, 115) * mm, "end": v(41.43, 115) * mm});
            skLineSegment(sketch, "E374", {"start": v(41.43, 118) * mm, "end": v(41.43, 115) * mm});
            skLineSegment(sketch, "E375", {"start": v(41.43, 118) * mm, "end": v(48.97, 118) * mm});
            skLineSegment(sketch, "E376", {"start": v(48.97, 118) * mm, "end": v(48.97, 115) * mm});
            skLineSegment(sketch, "E377", {"start": v(48.97, 115) * mm, "end": v(53.5, 115) * mm});
            skLineSegment(sketch, "E378", {"start": v(-53.5, 51) * mm, "end": v(-53.5, 55.78) * mm});
            skLineSegment(sketch, "E379", {"start": v(-53.5, 55.78) * mm, "end": v(-56.5, 55.78) * mm});
            skLineSegment(sketch, "E380", {"start": v(-56.5, 55.78) * mm, "end": v(-56.5, 63.56) * mm});
            skLineSegment(sketch, "E381", {"start": v(-53.5, 63.56) * mm, "end": v(-56.5, 63.56) * mm});
            skLineSegment(sketch, "E382", {"start": v(-53.5, 63.56) * mm, "end": v(-53.5, 71.33) * mm});
            skLineSegment(sketch, "E383", {"start": v(-53.5, 71.33) * mm, "end": v(-56.5, 71.33) * mm});
            skLineSegment(sketch, "E384", {"start": v(-56.5, 71.33) * mm, "end": v(-56.5, 79.11) * mm});
            skLineSegment(sketch, "E385", {"start": v(-53.5, 79.11) * mm, "end": v(-56.5, 79.11) * mm});
            skLineSegment(sketch, "E386", {"start": v(-53.5, 79.11) * mm, "end": v(-53.5, 86.89) * mm});
            skLineSegment(sketch, "E387", {"start": v(-53.5, 86.89) * mm, "end": v(-56.5, 86.89) * mm});
            skLineSegment(sketch, "E388", {"start": v(-56.5, 86.89) * mm, "end": v(-56.5, 94.67) * mm});
            skLineSegment(sketch, "E389", {"start": v(-53.5, 94.67) * mm, "end": v(-56.5, 94.67) * mm});
            skLineSegment(sketch, "E390", {"start": v(-53.5, 94.67) * mm, "end": v(-53.5, 102.44) * mm});
            skLineSegment(sketch, "E391", {"start": v(-53.5, 102.44) * mm, "end": v(-56.5, 102.44) * mm});
            skLineSegment(sketch, "E392", {"start": v(-56.5, 102.44) * mm, "end": v(-56.5, 110.22) * mm});
            skLineSegment(sketch, "E393", {"start": v(-53.5, 110.22) * mm, "end": v(-56.5, 110.22) * mm});
            skLineSegment(sketch, "E394", {"start": v(-53.5, 110.22) * mm, "end": v(-53.5, 115) * mm});
            skLineSegment(sketch, "E395", {"start": v(53.5, 51) * mm, "end": v(53.5, 55.78) * mm});
            skLineSegment(sketch, "E396", {"start": v(56.5, 55.78) * mm, "end": v(53.5, 55.78) * mm});
            skLineSegment(sketch, "E397", {"start": v(56.5, 55.78) * mm, "end": v(56.5, 63.56) * mm});
            skLineSegment(sketch, "E398", {"start": v(56.5, 63.56) * mm, "end": v(53.5, 63.56) * mm});
            skLineSegment(sketch, "E399", {"start": v(53.5, 63.56) * mm, "end": v(53.5, 71.33) * mm});
            skLineSegment(sketch, "E400", {"start": v(56.5, 71.33) * mm, "end": v(53.5, 71.33) * mm});
            skLineSegment(sketch, "E401", {"start": v(56.5, 71.33) * mm, "end": v(56.5, 79.11) * mm});
            skLineSegment(sketch, "E402", {"start": v(56.5, 79.11) * mm, "end": v(53.5, 79.11) * mm});
            skLineSegment(sketch, "E403", {"start": v(53.5, 79.11) * mm, "end": v(53.5, 86.89) * mm});
            skLineSegment(sketch, "E404", {"start": v(56.5, 86.89) * mm, "end": v(53.5, 86.89) * mm});
            skLineSegment(sketch, "E405", {"start": v(56.5, 86.89) * mm, "end": v(56.5, 94.67) * mm});
            skLineSegment(sketch, "E406", {"start": v(56.5, 94.67) * mm, "end": v(53.5, 94.67) * mm});
            skLineSegment(sketch, "E407", {"start": v(53.5, 94.67) * mm, "end": v(53.5, 102.44) * mm});
            skLineSegment(sketch, "E408", {"start": v(56.5, 102.44) * mm, "end": v(53.5, 102.44) * mm});
            skLineSegment(sketch, "E409", {"start": v(56.5, 102.44) * mm, "end": v(56.5, 110.22) * mm});
            skLineSegment(sketch, "E410", {"start": v(56.5, 110.22) * mm, "end": v(53.5, 110.22) * mm});
            skLineSegment(sketch, "E411", {"start": v(53.5, 110.22) * mm, "end": v(53.5, 115) * mm});
            skCircle(sketch, "E412", {"center": v(-21.5, -40) * mm, "radius": 23.77 * mm});
            skSolve(sketch);
        }
        {
            var Q0;
            Q0=qCreatedBy(makeId("Top.planeOp"),FACE);
            var sketch = newSketch(context, id + "F1", { "sketchPlane" : qUnion([Q0])});
            skText(sketch, "E413", { "text": "G.I.L.V.I.S.", "fontName": "AllertaStencil-Regular.ttf"});
            skText(sketch, "E414", { "text": "MK.1", "fontName": "AllertaStencil-Regular.ttf"});
            const initialGuessF1  = {"E413": [0.004, -0.03834, 1, 0, 0.00741], "E414": [0.035, -0.04415, 1, 0, 0.0048]};
            skSetInitialGuess(sketch, initialGuessF1);
            skSolve(sketch);
        }
        {
            var Q0;
            Q0 = qSketchRegion(id + "F0", true);
            extrude(context, id + "F2", {"entities" : qUnion([Q0]), "oppositeDirection" : true, "depth" : 3 * mm});
        }
        {
            var Q0;
            Q0 = qSketchRegion(id + "F1", true);
            extrude(context, id + "F3", {"entities" : qUnion([Q0]), "operationType" : NewBodyOperationType.REMOVE, "oppositeDirection" : true, "depth" : 1 * mm});
        }
    });
